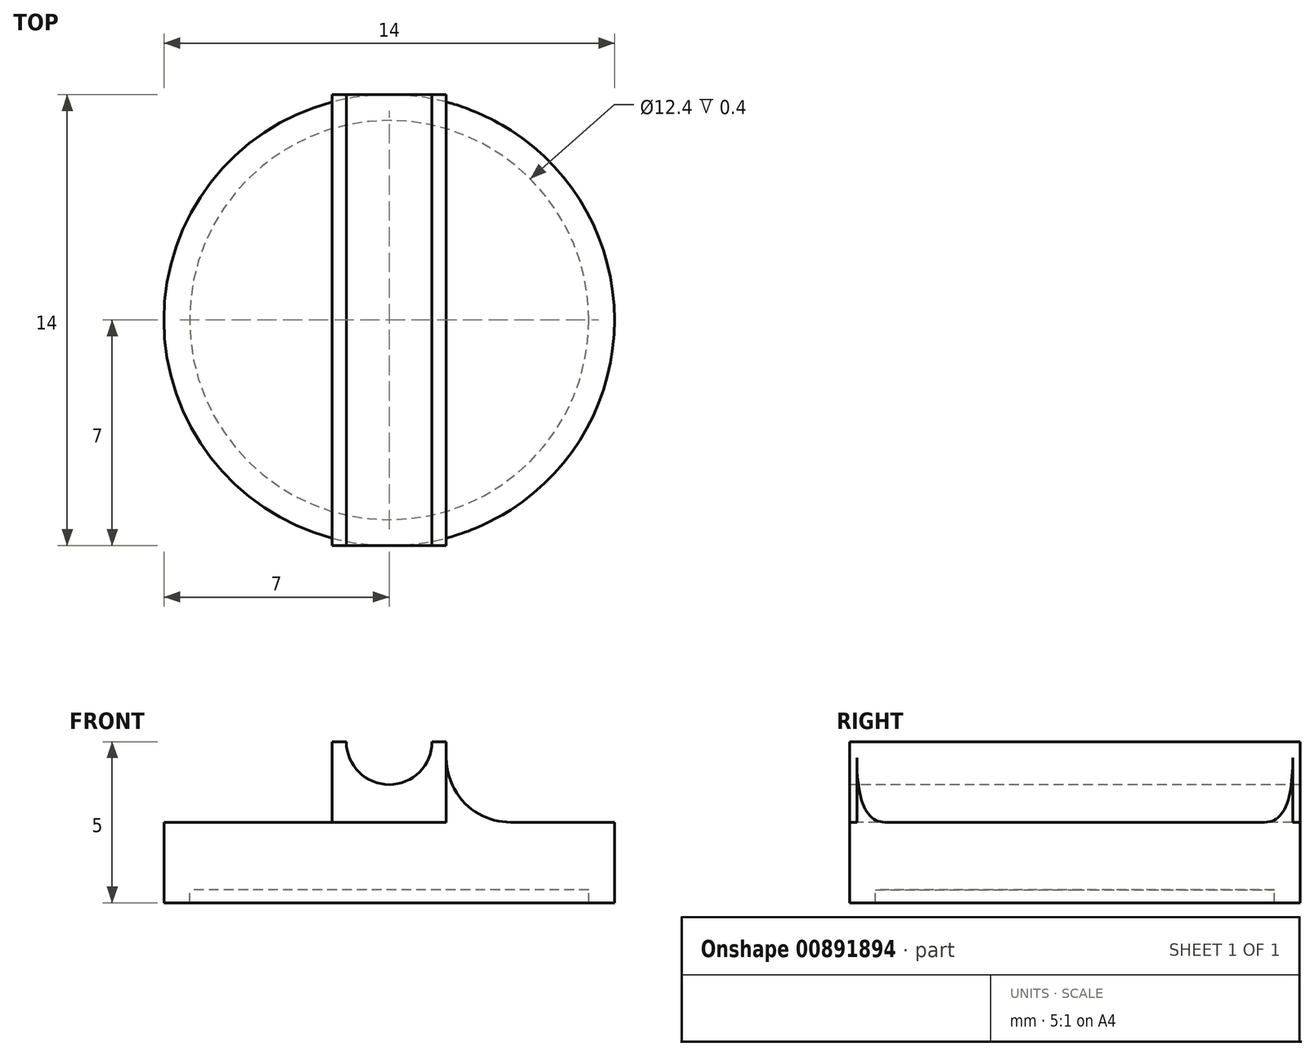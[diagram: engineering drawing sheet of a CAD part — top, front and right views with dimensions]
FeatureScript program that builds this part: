
annotation { "Feature Type Name" : "Feature", "Feature Type Description" : "" }
export const myFeature = defineFeature(function(context is Context, id is Id, definition is map)
    precondition{}
    {
        {
            var Q0;
            Q0=qCreatedBy(makeId("Front.planeOp"),FACE);
            var sketch = newSketch(context, id + "F0", { "sketchPlane" : qUnion([Q0])});
            skLineSegment(sketch, "E0.right", {"start": v(7, 0) * mm, "end": v(7, -2.5) * mm});
            skLineSegment(sketch, "E1.top", {"start": v(0, -2.1) * mm, "end": v(6.2, -2.1) * mm});
            skLineSegment(sketch, "E1.right", {"start": v(6.2, -2.5) * mm, "end": v(6.2, -2.1) * mm});
            skLineSegment(sketch, "E2", {"start": v(6.2, -2.5) * mm, "end": v(7, -2.5) * mm});
            skLineSegment(sketch, "E3", {"start": v(0, 0) * mm, "end": v(0, -2.1) * mm});
            skLineSegment(sketch, "E4", {"start": v(7, 0) * mm, "end": v(7, -1.05) * mm});
            skPoint(sketch, "E4.endSnap0", {"position": v(0, -1.05) * mm});
            skLineSegment(sketch, "E5", {"start": v(1.5, 0) * mm, "end": v(7, 0) * mm});
            skLineSegment(sketch, "E6", {"start": v(0, 0) * mm, "end": v(1.5, 0) * mm});
            skSolve(sketch);
        }
        {
            var Q0;
            Q0=makeQuery(id+"F0.imprint","IMPRINT",FACE,{"disambiguationData":[TD([[makeQuery(id+"F0.imprint","IMPRINT",EDGE,{"derivedFrom":sQuery(id+"F0.wireOp",EDGE,"E0.right")}),-1.0]])]});
            var Q1;
            Q1=sQuery(id+"F0.wireOp",EDGE,"E3");
            revolve(context, id + "F1", {"surfaceOperationType" : NewSurfaceOperationType.NEW, "entities" : qUnion([Q0]), "axis" : qUnion([Q1]), "revolveType" : RevolveType.FULL});
        }
        {
            var Q0;
            Q0=qCreatedBy(makeId("Front.planeOp"),FACE);
            var sketch = newSketch(context, id + "F2", { "sketchPlane" : qUnion([Q0])});
            skLineSegment(sketch, "E7", {"start": v(0, 0) * mm, "end": v(1.77, 0) * mm});
            skLineSegment(sketch, "E8", {"start": v(1.77, 0) * mm, "end": v(1.77, 2.5) * mm});
            skLineSegment(sketch, "E9", {"start": v(1.77, 2.5) * mm, "end": v(-1.77, 2.5) * mm});
            skLineSegment(sketch, "E10", {"start": v(0, 0) * mm, "end": v(-1.77, 0) * mm});
            skLineSegment(sketch, "E11", {"start": v(-1.77, 2.5) * mm, "end": v(-1.77, 0) * mm});
            skSolve(sketch);
        }
        {
            var Q0;
            Q0 = qSketchRegion(id + "F2", true);
            extrude(context, id + "F3", {"entities" : qUnion([Q0]), "operationType" : NewBodyOperationType.ADD, "endBound" : BoundingType.SYMMETRIC, "depth" : 6 * mm, "offsetDistance" : 25 * mm});
        }
        {
            var Q0;
            Q0=makeQuery(id+"F3.opExtrude","CAP_FACE",FACE,{"disambiguationData":[OSD([sQuery(id+"F2.wireOp",EDGE,"E7"),sQuery(id+"F2.wireOp",EDGE,"E8"),sQuery(id+"F2.wireOp",EDGE,"E9"),sQuery(id+"F2.wireOp",EDGE,"E10"),sQuery(id+"F2.wireOp",EDGE,"E11")])],"isStart":false});
            var sketch = newSketch(context, id + "F4", { "sketchPlane" : qUnion([Q0])});
            skCircle(sketch, "E12", {"center": v(0, 2.5) * mm, "radius": 1.33 * mm});
            skSolve(sketch);
        }
        {
            var Q0;
            Q0 = qSketchRegion(id + "F4", true);
            extrude(context, id + "F5", {"entities" : qUnion([Q0]), "operationType" : NewBodyOperationType.REMOVE, "endBound" : BoundingType.SYMMETRIC, "oppositeDirection" : true, "depth" : 25 * mm, "offsetDistance" : 25 * mm});
        }
        {
            var Q0;
            Q0=makeQuery(id+"F3.opExtrude","CAP_FACE",FACE,{"disambiguationData":[OSD([sQuery(id+"F2.wireOp",EDGE,"E7"),sQuery(id+"F2.wireOp",EDGE,"E8"),sQuery(id+"F2.wireOp",EDGE,"E9"),sQuery(id+"F2.wireOp",EDGE,"E10"),sQuery(id+"F2.wireOp",EDGE,"E11")])],"isStart":false});
            extrude(context, id + "F6", {"entities" : qUnion([Q0]), "operationType" : NewBodyOperationType.ADD, "depth" : 4 * mm, "offsetDistance" : 25 * mm});
        }
        {
            var Q0;
            Q0=makeQuery(id+"F3.opExtrude","CAP_FACE",FACE,{"disambiguationData":[OSD([sQuery(id+"F2.wireOp",EDGE,"E7"),sQuery(id+"F2.wireOp",EDGE,"E8"),sQuery(id+"F2.wireOp",EDGE,"E9"),sQuery(id+"F2.wireOp",EDGE,"E10"),sQuery(id+"F2.wireOp",EDGE,"E11")])],"isStart":true});
            extrude(context, id + "F7", {"entities" : qUnion([Q0]), "operationType" : NewBodyOperationType.ADD, "depth" : 4 * mm, "offsetDistance" : 25 * mm});
        }
        {
            var Q0;
            {var subQ0=sQuery(id+"F2.wireOp",EDGE,"E8");var subQ1=sQuery(id+"F2.wireOp",EDGE,"E7");Q0=makeQuery(id+"F7.boolean.opBoolean","MERGE",EDGE,{"derivedFrom":[makeQuery(id+"F6.boolean.opBoolean","MERGE",EDGE,{"derivedFrom":[makeQuery(id+"F3.opExtrude","SWEPT_EDGE",EDGE,{"disambiguationData":[OSD([subQ1,subQ0])]}),makeQuery(id+"F6.opExtrude","SWEPT_EDGE",EDGE,{"disambiguationData":[OSD([subQ1,subQ0])]})]}),makeQuery(id+"F7.opExtrude","SWEPT_EDGE",EDGE,{"disambiguationData":[OSD([subQ1,subQ0])]})]});}
            var Q1;
            {var subQ0=sQuery(id+"F2.wireOp",EDGE,"E11");var subQ1=sQuery(id+"F2.wireOp",EDGE,"E10");Q1=makeQuery(id+"F7.boolean.opBoolean","MERGE",EDGE,{"derivedFrom":[makeQuery(id+"F6.boolean.opBoolean","MERGE",EDGE,{"derivedFrom":[makeQuery(id+"F3.opExtrude","SWEPT_EDGE",EDGE,{"disambiguationData":[OSD([subQ1,subQ0])]}),makeQuery(id+"F6.opExtrude","SWEPT_EDGE",EDGE,{"disambiguationData":[OSD([subQ1,subQ0])]})]}),makeQuery(id+"F7.opExtrude","SWEPT_EDGE",EDGE,{"disambiguationData":[OSD([subQ1,subQ0])]})]});}
            fillet(context, id + "F8", {"entities" : qUnion([Q0, Q1]), "radius" : 2 * mm, "tangentPropagation" : true, "allowEdgeOverflow" : false});
        }
    });
